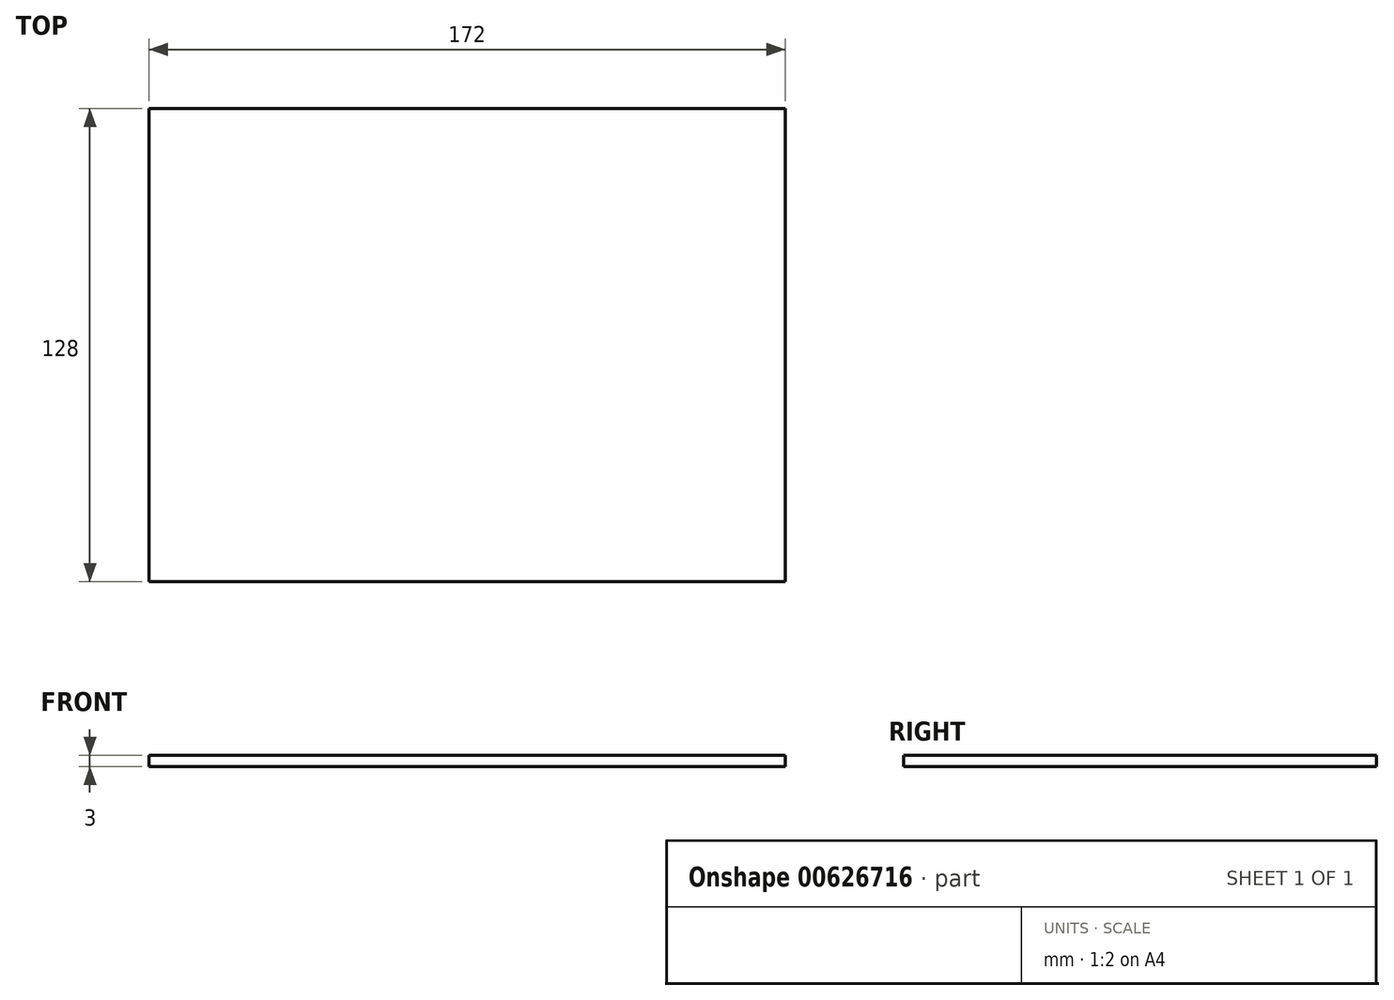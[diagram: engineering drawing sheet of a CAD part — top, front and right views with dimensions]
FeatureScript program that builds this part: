
annotation { "Feature Type Name" : "Feature", "Feature Type Description" : "" }
export const myFeature = defineFeature(function(context is Context, id is Id, definition is map)
    precondition{}
    {
        {
            var Q0;
            Q0=qCreatedBy(makeId("Top.planeOp"),FACE);
            var sketch = newSketch(context, id + "F0", { "sketchPlane" : qUnion([Q0])});
            skLineSegment(sketch, "E0.bottom", {"start": v(-86, 64) * mm, "end": v(86, 64) * mm});
            skLineSegment(sketch, "E0.top", {"start": v(-86, -64) * mm, "end": v(86, -64) * mm});
            skLineSegment(sketch, "E0.left", {"start": v(-86, 64) * mm, "end": v(-86, -64) * mm});
            skLineSegment(sketch, "E0.right", {"start": v(86, 64) * mm, "end": v(86, -64) * mm});
            skPoint(sketch, "E0.middle", {"position": v(0, 0) * mm});
            skSolve(sketch);
        }
        {
            var Q0;
            Q0=makeQuery(id+"F0.imprint","IMPRINT",FACE,{"disambiguationData":[TD([[makeQuery(id+"F0.imprint","IMPRINT",EDGE,{"derivedFrom":sQuery(id+"F0.wireOp",EDGE,"E0.bottom")}),-1.0]])]});
            extrude(context, id + "F1", {"entities" : qUnion([Q0]), "depth" : 3 * mm, "offsetDistance" : 25 * mm});
        }
    });
